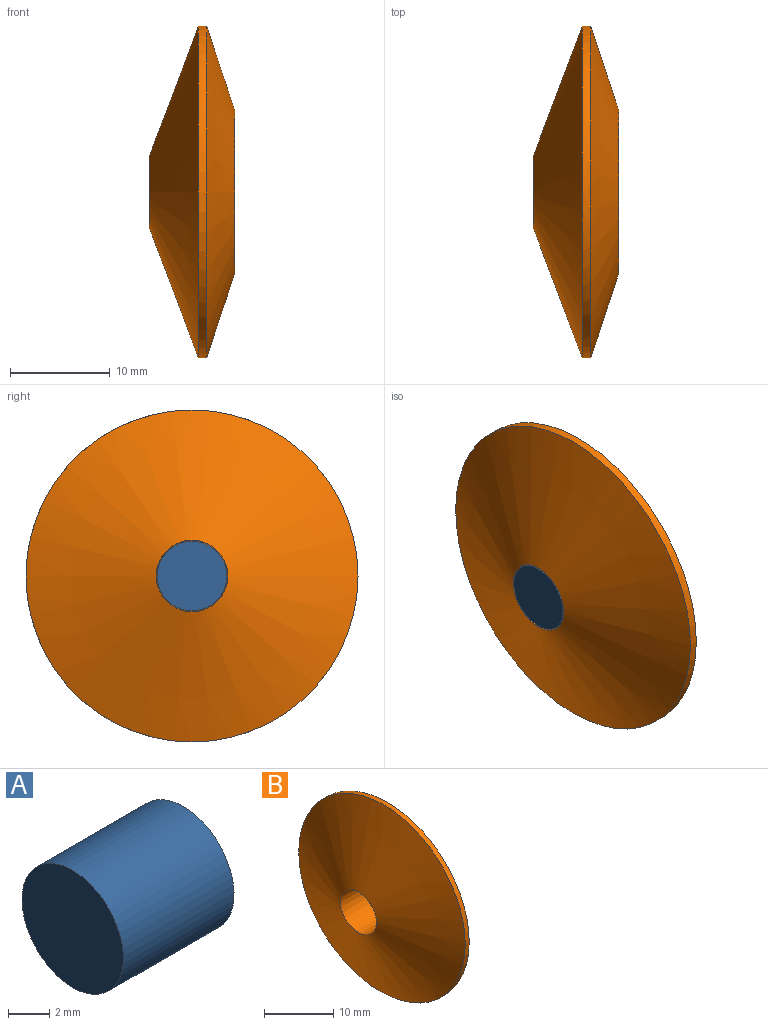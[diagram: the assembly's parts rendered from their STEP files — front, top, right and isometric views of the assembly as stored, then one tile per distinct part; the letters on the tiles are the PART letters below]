
ASSEMBLY  parts=2 mates=1
PART A: 3 faces, bbox 7.6x7x7 mm
  f0: cylinder r=3.49mm len=7.62mm, axis (-1,0,0), area 167.2mm2, adj f1,f2
  f1: plane 6.99x6.99mm, normal (1,0,0), area 38.3mm2, adj f0
  f2: plane 6.99x6.99mm, normal (-1,0,0), area 38.3mm2, adj f0
PART B: 5 faces, bbox 8.8x33.3x33.3 mm
  f0: cone r=17.85mm half-angle=71.7deg, axis (-1,-0.02,0), area 693.1mm2, adj f3,f4
  f1: cone r=17.85mm half-angle=69.4deg, axis (1,0.02,0), area 888.1mm2, adj f2,f4
  f2: cone r=3.6mm half-angle=1.1deg, axis (-1,-0.02,0), area 113.2mm2, adj f1,f3
  f3: cone r=8.22mm half-angle=53.6deg, axis (1,0.02,0), area 215.8mm2, adj f0,f2
  f4: cone r=16.66mm half-angle=1.1deg, axis (-1,-0.02,0), area 88.7mm2, adj f0,f1
PLACE A at identity
PLACE B rot(axis=(0,0,-1),1.1deg) t=(5.12,69.7,-9.71)mm
MATE fastened B.f2 <-> A.f0  axis (-1,0,0) through (0,64.38,-9.71)mm
